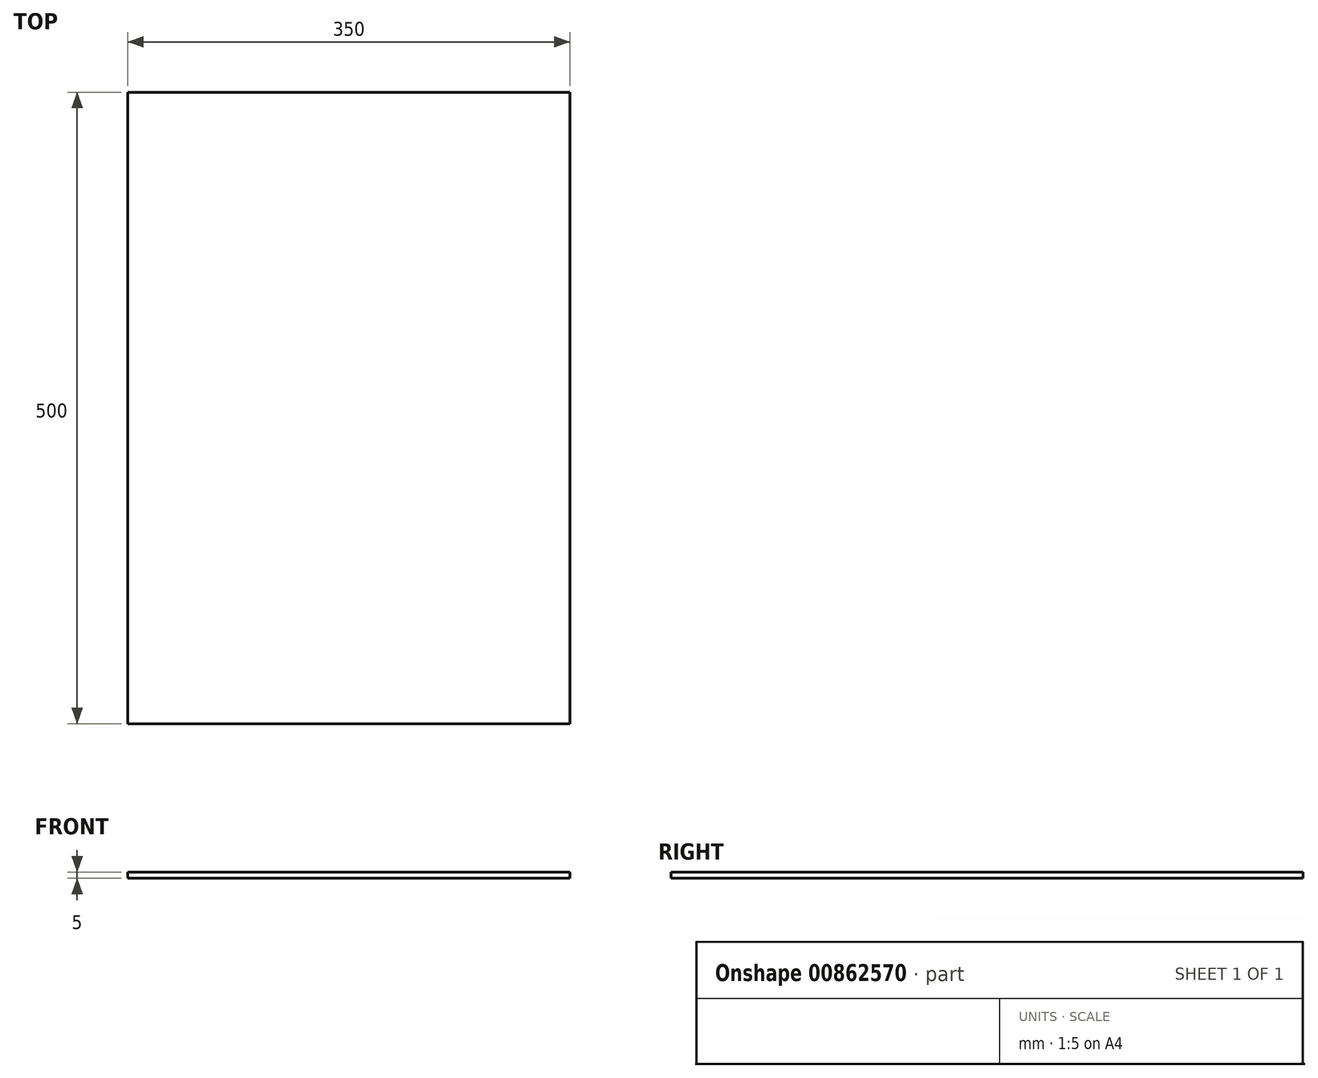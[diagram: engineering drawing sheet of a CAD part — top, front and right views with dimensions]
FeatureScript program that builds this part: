
annotation { "Feature Type Name" : "Feature", "Feature Type Description" : "" }
export const myFeature = defineFeature(function(context is Context, id is Id, definition is map)
    precondition{}
    {
        {
            var Q0;
            Q0=qCreatedBy(makeId("Top.planeOp"),FACE);
            var sketch = newSketch(context, id + "F0", { "sketchPlane" : qUnion([Q0])});
            skLineSegment(sketch, "E0.bottom", {"start": v(175, -250) * mm, "end": v(-175, -250) * mm});
            skLineSegment(sketch, "E0.top", {"start": v(175, 250) * mm, "end": v(-175, 250) * mm});
            skLineSegment(sketch, "E0.left", {"start": v(175, -250) * mm, "end": v(175, 250) * mm});
            skLineSegment(sketch, "E0.right", {"start": v(-175, -250) * mm, "end": v(-175, 250) * mm});
            skPoint(sketch, "E0.middle", {"position": v(0, 0) * mm});
            skLineSegment(sketch, "E1", {"start": v(-410.69, 0) * mm, "end": v(486.82, 0) * mm});
            skLineSegment(sketch, "E2", {"start": v(0, 385.2) * mm, "end": v(0, -375.78) * mm});
            skSolve(sketch);
        }
        {
            var Q0;
            Q0 = qSketchRegion(id + "F0", true);
            extrude(context, id + "F1", {"entities" : qUnion([Q0]), "depth" : 5 * mm, "offsetDistance" : 25 * mm});
        }
    });
